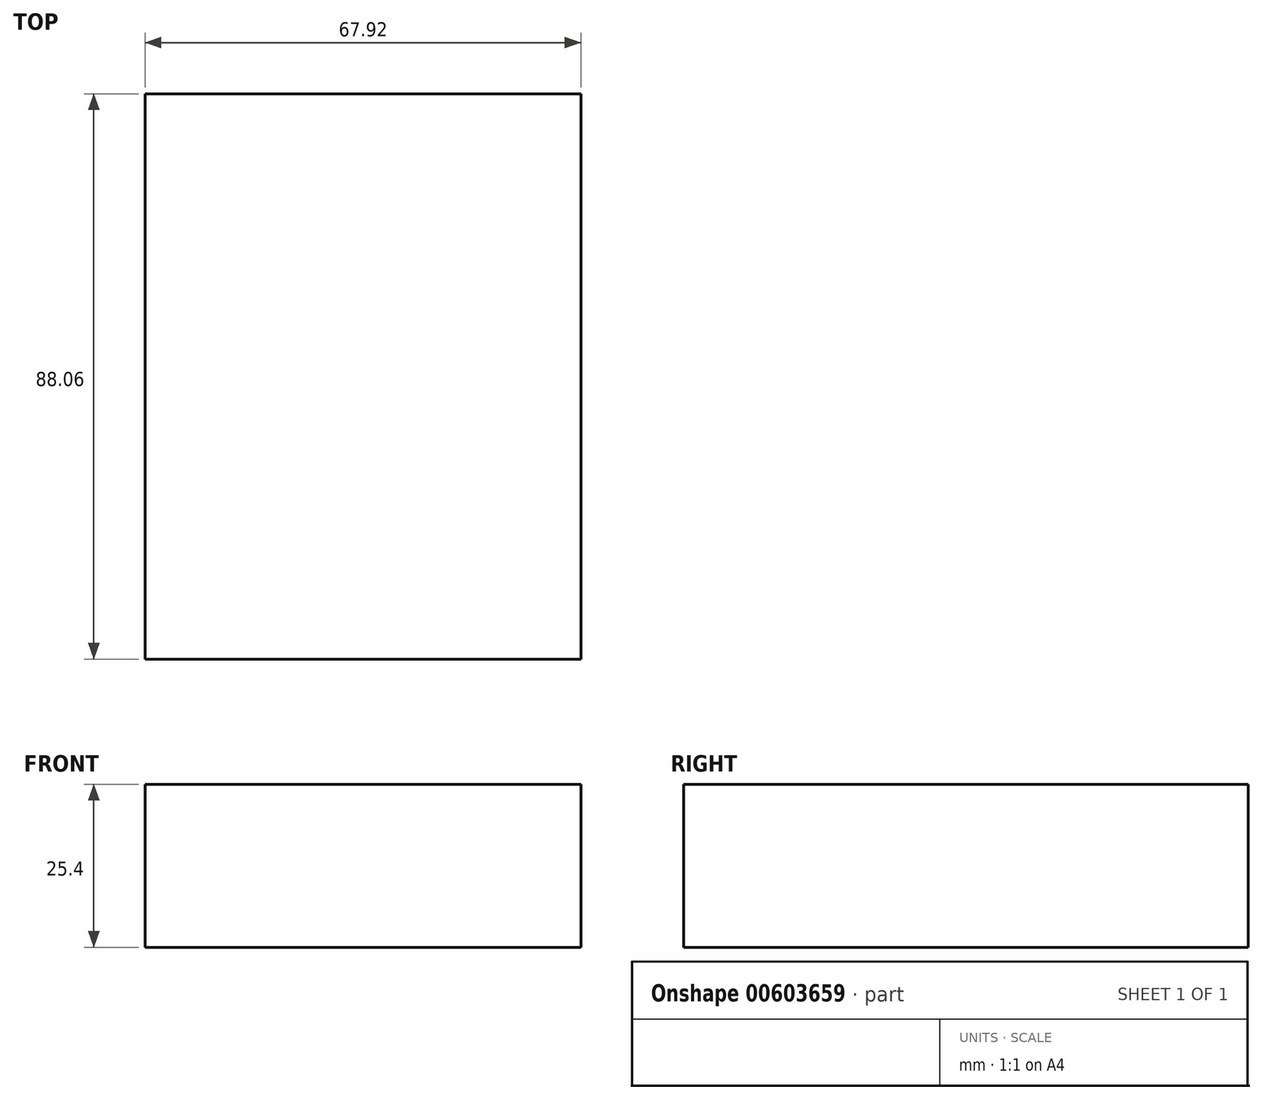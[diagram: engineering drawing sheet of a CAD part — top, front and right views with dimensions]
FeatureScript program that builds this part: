
annotation { "Feature Type Name" : "Feature", "Feature Type Description" : "" }
export const myFeature = defineFeature(function(context is Context, id is Id, definition is map)
    precondition{}
    {
        {
            var Q0;
            Q0=qCreatedBy(makeId("Top.planeOp"),FACE);
            var sketch = newSketch(context, id + "F0", { "sketchPlane" : qUnion([Q0])});
            skLineSegment(sketch, "E0.bottom", {"start": v(33.96, 44.03) * mm, "end": v(-33.96, 44.03) * mm});
            skLineSegment(sketch, "E0.top", {"start": v(33.96, -44.03) * mm, "end": v(-33.96, -44.03) * mm});
            skLineSegment(sketch, "E0.left", {"start": v(33.96, 44.03) * mm, "end": v(33.96, -44.03) * mm});
            skLineSegment(sketch, "E0.right", {"start": v(-33.96, 44.03) * mm, "end": v(-33.96, -44.03) * mm});
            skPoint(sketch, "E0.middle", {"position": v(0, 0) * mm});
            skSolve(sketch);
        }
        {
            var Q0;
            Q0=makeQuery(id+"F0.imprint","IMPRINT",FACE,{"disambiguationData":[TD([[makeQuery(id+"F0.imprint","IMPRINT",EDGE,{"derivedFrom":sQuery(id+"F0.wireOp",EDGE,"E0.bottom")}),1.0]])]});
            extrude(context, id + "F1", {"entities" : qUnion([Q0]), "depth" : 25.4 * mm, "offsetDistance" : 25.4 * mm});
        }
    });
